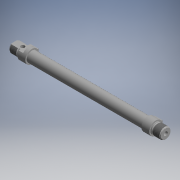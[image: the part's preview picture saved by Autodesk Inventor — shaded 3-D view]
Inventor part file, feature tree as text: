
AUTODESK INVENTOR PART (.ipt)
format: ipt  version: 2017.3 (Build 213256000, 256)  size: 278,528 bytes
history: native  units: mm (DEFAULTED — no unit token found)
features: other x70, sketch x10, revolve x4, extrude x3, hole x3, thread x2
ambient origin geometry x8: Origin, YZ Plane, XZ Plane, XY Plane, X Axis, Y Axis, Z Axis, Center Point
bodies: Solid1 (feature_tree)
feature tree (92):
  revolve  "Revolution1"  [1 undecoded]
  thread  "Thread1"  [1 undecoded]
  extrude  "Extrusion1"  Depth=16.0mm TaperAngle=0.0deg
  revolve  "Revolution2"  [1 undecoded]
  extrude  "Extrusion2"  TaperAngle=360.0deg  [1 undecoded]
  revolve  "Revolution3"  [1 undecoded]
  thread  "Thread2"  [1 undecoded]
  extrude  "Extrusion3"  [1 undecoded]
  hole  "Hole1"  [1 undecoded]
  hole  "Hole2"  [1 undecoded]
  hole  "Hole3"  [1 undecoded]
  revolve  "Revolution4"  [1 undecoded]
  other  "FDT_FRONT_XY"
  other  "FDT_FRONT_YZ"
  other  "FDT_FRONT_ZX"
  other  "FDT_FRONT_X"
  other  "FDT_FRONT_Y"
  other  "FDT_FRONT_Z"
  other  "FDT_FRONT_Center"
  other  "FDT_QSFRONT_XY"
  other  "FDT_QSFRONT_YZ"
  other  "FDT_QSFRONT_ZX"
  other  "FDT_QSFRONT_X"
  other  "FDT_QSFRONT_Y"
  other  "FDT_QSFRONT_Z"
  other  "FDT_QSFRONT_Center"
  other  "FDT_QSREAR_XY"
  other  "FDT_QSREAR_YZ"
  other  "FDT_QSREAR_ZX"
  other  "FDT_QSREAR_X"
  other  "FDT_QSREAR_Y"
  other  "FDT_QSREAR_Z"
  other  "FDT_QSREAR_Center"
  other  "FDT_REAR_XY"
  other  "FDT_REAR_YZ"
  other  "FDT_REAR_ZX"
  other  "FDT_REAR_X"
  other  "FDT_REAR_Y"
  other  "FDT_REAR_Z"
  other  "FDT_REAR_Center"
  other  "FDT_SMBR1_XY"
  other  "FDT_SMBR1_YZ"
  other  "FDT_SMBR1_ZX"
  other  "FDT_SMBR1_X"
  other  "FDT_SMBR1_Y"
  other  "FDT_SMBR1_Z"
  other  "FDT_SMBR1_Center"
  other  "FDT_SMBR2_XY"
  other  "FDT_SMBR2_YZ"
  other  "FDT_SMBR2_ZX"
  other  "FDT_SMBR2_X"
  other  "FDT_SMBR2_Y"
  other  "FDT_SMBR2_Z"
  other  "FDT_SMBR2_Center"
  other  "FDT_SWIVELAXIS_XY"
  other  "FDT_SWIVELAXIS_YZ"
  other  "FDT_SWIVELAXIS_ZX"
  other  "FDT_SWIVELAXIS_X"
  other  "FDT_SWIVELAXIS_Y"
  other  "FDT_SWIVELAXIS_Z"
  other  "FDT_SWIVELAXIS_Center"
  other  "NUT_XY"
  other  "NUT_YZ"
  other  "NUT_ZX"
  other  "NUT_X"
  other  "NUT_Y"
  other  "NUT_Z"
  other  "NUT_Center"
  other  "ZR_XY"
  other  "ZR_YZ"
  other  "ZR_ZX"
  other  "ZR_X"
  other  "ZR_Y"
  other  "ZR_Z"
  other  "ZR_Center"
  other  "ZYL_XY"
  other  "ZYL_YZ"
  other  "ZYL_ZX"
  other  "ZYL_X"
  other  "ZYL_Y"
  other  "ZYL_Z"
  other  "ZYL_Center"
  sketch  "Sketch_1"  dims[d0=360.0deg d1=12.95mm d2=0.0mm d3=16.0mm d4=0.0mm]
  sketch  "Sketch_2"  dims[d5=360.0deg d6=16.0mm d7=0.0mm]
  sketch  "Sketch_3"  dims[d8=360.0deg d9=12.95mm d10=0.0mm]
  sketch  "Sketch_16"  dims[d35=0.0mm d36=0.0mm d37=0.0mm d38=0.0mm d39=0.0mm d40=0.0mm]
  sketch  "Sketch_23"
  sketch  "Sketch_6"  dims[d11=27.0mm d12=0.0mm]
  sketch  "Sketch7"  dims[d13=8.0mm d14=6.0mm d15=4.0mm d16=2.0mm d17=90.0deg d18=16.0mm d19=0.0mm]
  sketch  "Sketch8"  dims[d20=8.566mm d21=10.081mm d22=9.728mm d23=2.0mm d24=90.0deg d25=13.5mm d26=0.0mm]
  sketch  "Sketch9"  dims[d27=8.566mm d28=8.581mm d29=9.728mm d30=2.0mm d31=90.0deg d32=16.0mm d33=120.0deg d34=360.0deg]
  sketch  "Sketch_64"
note: 11 required parameter values undecoded (feature->parameter linkage not recoverable at this tier; creation-order binding heuristic only, values carry confidence <= 0.55)